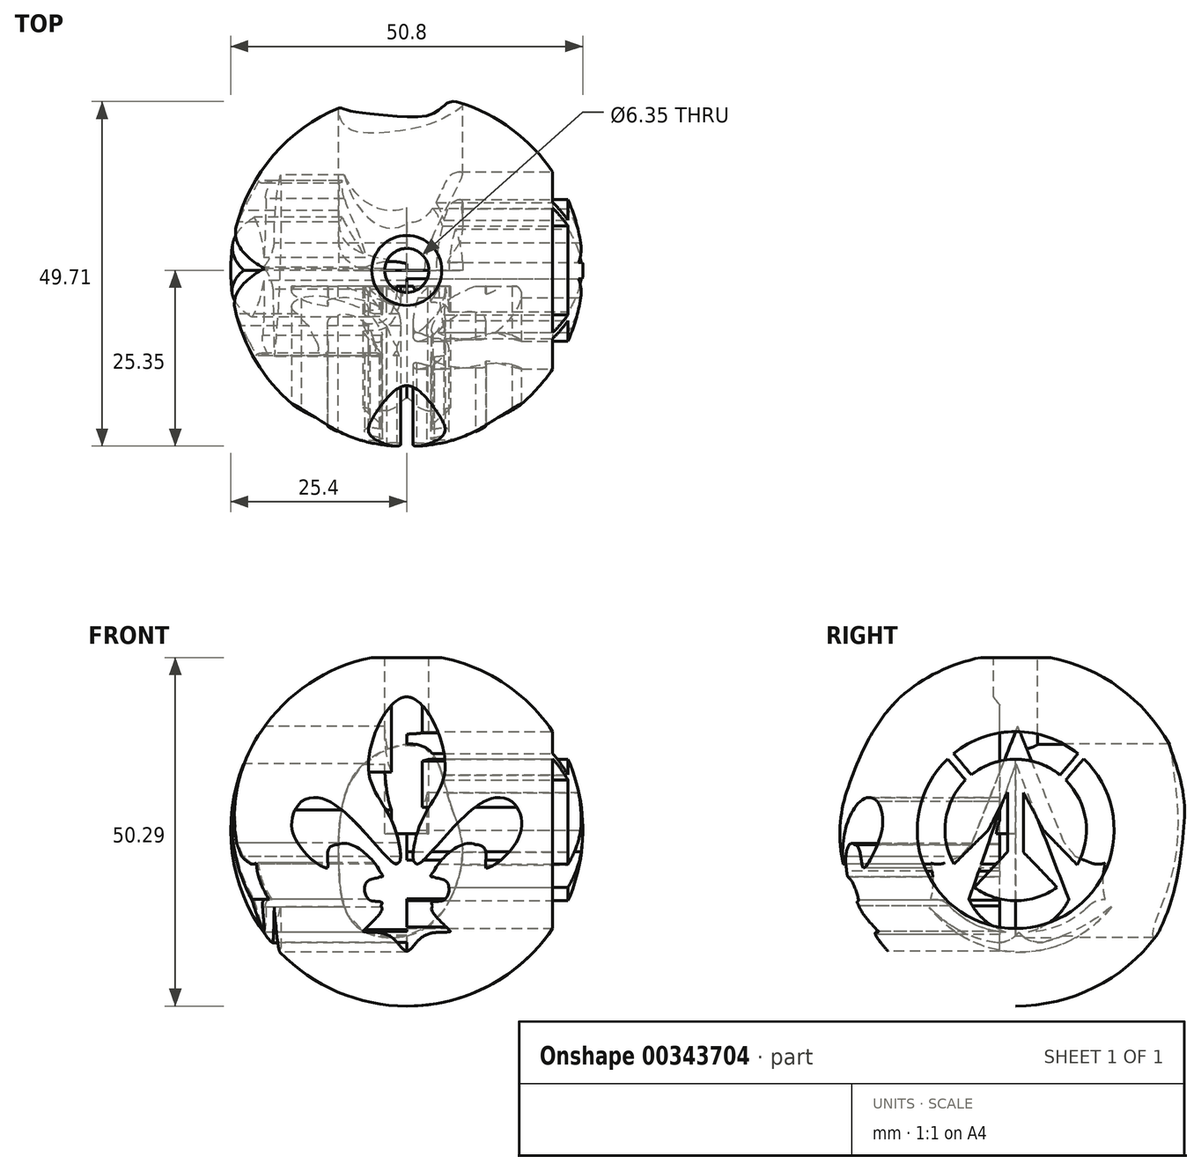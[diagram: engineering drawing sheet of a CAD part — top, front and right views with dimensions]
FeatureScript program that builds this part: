
annotation { "Feature Type Name" : "Feature", "Feature Type Description" : "" }
export const myFeature = defineFeature(function(context is Context, id is Id, definition is map)
    precondition{}
    {
        {
            var Q0;
            Q0=qCreatedBy(makeId("Front.planeOp"),FACE);
            var sketch = newSketch(context, id + "F0", { "sketchPlane" : qUnion([Q0])});
            skArc(sketch, "E0", {"start": v(0, 25.4) * mm, "mid": v(-25.4, 0) * mm, "end": v(0, -25.4) * mm});
            skLineSegment(sketch, "E1", {"start": v(0, 25.4) * mm, "end": v(0, -25.4) * mm});
            skPoint(sketch, "E2.orphan", {"position": v(0, 39.72) * mm});
            skSolve(sketch);
        }
        {
            var Q0;
            Q0=qCreatedBy(makeId("Top.planeOp"),FACE);
            var sketch = newSketch(context, id + "F1", { "sketchPlane" : qUnion([Q0])});
            skCircle(sketch, "E3", {"center": v(0, 0) * mm, "radius": 25.4 * mm});
            skSolve(sketch);
        }
        {
            var Q0;
            Q0=makeQuery(id+"F0.imprint","IMPRINT",FACE,{"disambiguationData":[TD([[makeQuery(id+"F0.imprint","IMPRINT",EDGE,{"derivedFrom":sQuery(id+"F0.wireOp",EDGE,"E0")}),1.0]])]});
            var Q1;
            Q1=sQuery(id+"F1.wireOp",EDGE,"E3");
            revolve(context, id + "F2", {"entities" : qUnion([Q0]), "axis" : qUnion([Q1]), "revolveType" : RevolveType.FULL});
        }
        {
            var Q0;
            Q0=qCreatedBy(makeId("Top.planeOp"),FACE);
            cPlane(context, id + "F3", {"entities" : qUnion([Q0]), "cplaneType" : CPlaneType.OFFSET, "offset" : 24.9 * mm, "width" : 152.4 * mm, "height" : 152.4 * mm});
        }
        {
            var Q0;
            Q0=qCreatedBy(id+"F3.planeOp",FACE);
            var sketch = newSketch(context, id + "F4", { "sketchPlane" : qUnion([Q0])});
            skLineSegment(sketch, "E4.bottom", {"start": v(-8.92, 8.63) * mm, "end": v(8.92, 8.63) * mm});
            skLineSegment(sketch, "E4.top", {"start": v(-8.92, -8.63) * mm, "end": v(8.92, -8.63) * mm});
            skLineSegment(sketch, "E4.left", {"start": v(-8.92, 8.63) * mm, "end": v(-8.92, -8.63) * mm});
            skLineSegment(sketch, "E4.right", {"start": v(8.92, 8.63) * mm, "end": v(8.92, -8.63) * mm});
            skPoint(sketch, "E4.middle", {"position": v(0, 0) * mm});
            skSolve(sketch);
        }
        {
            var Q0;
            Q0=makeQuery(id+"F4.imprint","IMPRINT",FACE,{"disambiguationData":[TD([[makeQuery(id+"F4.imprint","IMPRINT",EDGE,{"derivedFrom":sQuery(id+"F4.wireOp",EDGE,"E4.bottom")}),-1.0]])]});
            extrude(context, id + "F5", {"entities" : qUnion([Q0]), "operationType" : NewBodyOperationType.REMOVE, "depth" : 30.23 * mm});
        }
        {
            var Q0;
            Q0=qCreatedBy(makeId("Front.planeOp"),FACE);
            cPlane(context, id + "F6", {"entities" : qUnion([Q0]), "cplaneType" : CPlaneType.OFFSET, "offset" : 25.4 * mm, "width" : 152.4 * mm, "height" : 152.4 * mm});
        }
        {
            var Q0;
            Q0=qCreatedBy(id+"F6.planeOp",FACE);
            var sketch = newSketch(context, id + "F7", { "sketchPlane" : qUnion([Q0])});
            skFitSpline(sketch, "E5", {"points": [v(0, 19.2) * mm, v(-5.54, 9.35) * mm, v(-2.06, 1.1) * mm, v(-1.4, -4.9) * mm, v(-12.3, 4.57) * mm, v(-16.9, 0) * mm, v(-11.64, -5.75) * mm, v(-11.35, -3.03) * mm, v(-8.82, -2.38) * mm, v(-3.47, -6.7) * mm, v(-5.35, -6.88) * mm, v(-5.63, -9.98) * mm, v(-3.57, -10.54) * mm, v(-6.47, -14.39) * mm, v(-3, -15.04) * mm, v(0, -17.48) * mm, v(3, -15.04) * mm, v(6.57, -15.04) * mm, v(3.57, -11.38) * mm, v(5.54, -9.98) * mm, v(5.63, -7.35) * mm, v(3.85, -6.6) * mm, v(7.6, -2.28) * mm, v(10.6, -2.84) * mm, v(11.07, -5.47) * mm, v(16.51, 0) * mm, v(12.2, 4.85) * mm, v(1.5, -4.9) * mm, v(2.25, 1.28) * mm, v(5.54, 9.45) * mm, v(0, 19.2) * mm]});
            skFitSpline(sketch, "E6.MirrorC", {"points": [v(0, 19.2) * mm, v(5.54, 9.35) * mm, v(2.06, 1.1) * mm, v(1.4, -4.9) * mm, v(12.3, 4.57) * mm, v(16.9, 0) * mm, v(11.64, -5.75) * mm, v(11.35, -3.03) * mm, v(8.82, -2.38) * mm, v(3.47, -6.7) * mm, v(5.35, -6.88) * mm, v(5.63, -9.98) * mm, v(3.57, -10.54) * mm, v(6.47, -14.39) * mm, v(3, -15.04) * mm, v(0, -17.48) * mm, v(-3, -15.04) * mm, v(-6.57, -15.04) * mm, v(-3.57, -11.38) * mm, v(-5.54, -9.98) * mm, v(-5.63, -7.35) * mm, v(-3.85, -6.6) * mm, v(-7.6, -2.28) * mm, v(-10.6, -2.84) * mm, v(-11.07, -5.47) * mm, v(-16.51, 0) * mm, v(-12.2, 4.85) * mm, v(-1.5, -4.9) * mm, v(-2.25, 1.28) * mm, v(-5.54, 9.45) * mm, v(0, 19.2) * mm]});
            skSolve(sketch);
        }
        {
            var Q0;
            {var subQ1=sQuery(id+"F7.wireOp",EDGE,"E5");Q0=makeQuery(id+"F7.imprint","IMPRINT",FACE,{"disambiguationData":[TD([[makeQuery(id+"F7.imprint","IMPRINT",EDGE,{"derivedFrom":subQ1}),1.0]])]});}
            extrude(context, id + "F8", {"entities" : qUnion([Q0]), "operationType" : NewBodyOperationType.REMOVE, "oppositeDirection" : true, "depth" : 23.1 * mm});
        }
        {
            var Q0;
            Q0=qCreatedBy(makeId("Right.planeOp"),FACE);
            cPlane(context, id + "F9", {"entities" : qUnion([Q0]), "cplaneType" : CPlaneType.OFFSET, "offset" : 25.4 * mm, "width" : 152.4 * mm, "height" : 152.4 * mm});
        }
        {
            var Q0;
            Q0=qCreatedBy(id+"F9.planeOp",FACE);
            var sketch = newSketch(context, id + "F10", { "sketchPlane" : qUnion([Q0])});
            skArc(sketch, "E7", {"start": v(-9.82, 10.27) * mm, "mid": v(0, -14.2) * mm, "end": v(9.8, 10.28) * mm});
            skPoint(sketch, "E7.first.point", {"position": v(-6.94, 12.4) * mm});
            skPoint(sketch, "E7.second.point", {"position": v(6.62, -12.57) * mm});
            skPoint(sketch, "E7.third.point", {"position": v(-8.96, -11.02) * mm});
            skArc(sketch, "E8", {"start": v(-7.24, 7.2) * mm, "mid": v(0, -10.2) * mm, "end": v(7.23, 7.2) * mm});
            skLineSegment(sketch, "E9", {"start": v(8.87, -5.03) * mm, "end": v(3.98, 0) * mm});
            skLineSegment(sketch, "E10", {"start": v(3.98, 0) * mm, "end": v(1.13, 5.4) * mm});
            skLineSegment(sketch, "E11", {"start": v(1.13, 5.4) * mm, "end": v(1.13, -3.2) * mm});
            skLineSegment(sketch, "E12", {"start": v(1.13, -3.2) * mm, "end": v(5.97, -8.27) * mm});
            skLineSegment(sketch, "E13", {"start": v(-8.96, 11.03) * mm, "end": v(-6.38, 7.96) * mm});
            skLineSegment(sketch, "E14", {"start": v(-9.82, 10.27) * mm, "end": v(-7.24, 7.2) * mm});
            skLineSegment(sketch, "E15", {"start": v(8.99, 11) * mm, "end": v(6.4, 7.94) * mm});
            skLineSegment(sketch, "E16", {"start": v(9.8, 10.28) * mm, "end": v(7.23, 7.2) * mm});
            skPoint(sketch, "E17.start.orphan", {"position": v(-3.94, 0) * mm});
            skLineSegment(sketch, "E18", {"start": v(-8.93, -4.94) * mm, "end": v(-3.94, 0) * mm});
            skLineSegment(sketch, "E19", {"start": v(-3.94, 0) * mm, "end": v(-1.18, 5.45) * mm});
            skLineSegment(sketch, "E20", {"start": v(-1.18, 5.45) * mm, "end": v(-1.18, -3.15) * mm});
            skLineSegment(sketch, "E21", {"start": v(-5.97, -8.27) * mm, "end": v(-1.18, -3.15) * mm});
            skArc(sketch, "E22.trimOffspring", {"start": v(6.4, 7.94) * mm, "mid": v(0.01, 10.2) * mm, "end": v(-6.38, 7.96) * mm});
            skArc(sketch, "E23.trimOffspring", {"start": v(8.99, 11) * mm, "mid": v(0.02, 14.2) * mm, "end": v(-8.96, 11.03) * mm});
            skSolve(sketch);
        }
        {
            var Q0;
            Q0=makeQuery(id+"F10.imprint","IMPRINT",FACE,{"disambiguationData":[TD([[makeQuery(id+"F10.imprint","IMPRINT",EDGE,{"derivedFrom":sQuery(id+"F10.wireOp",EDGE,"E13")}),1.0]])]});
            var Q1;
            Q1=makeQuery(id+"F10.imprint","IMPRINT",FACE,{"disambiguationData":[TD([[makeQuery(id+"F10.imprint","IMPRINT",EDGE,{"derivedFrom":sQuery(id+"F10.wireOp",EDGE,"E7")}),1.0]])]});
            var Q2;
            {var subQ0=sQuery(id+"F10.wireOp",EDGE,"E18");Q2=makeQuery(id+"F10.imprint","IMPRINT",FACE,{"disambiguationData":[TD([[makeQuery(id+"F10.imprint","IMPRINT",EDGE,{"derivedFrom":subQ0}),-1.0]])]});}
            var Q3;
            {var subQ0=sQuery(id+"F10.wireOp",EDGE,"E9");Q3=makeQuery(id+"F10.imprint","IMPRINT",FACE,{"disambiguationData":[TD([[makeQuery(id+"F10.imprint","IMPRINT",EDGE,{"derivedFrom":subQ0}),1.0]])]});}
            extrude(context, id + "F11", {"entities" : qUnion([Q0, Q1, Q2, Q3]), "operationType" : NewBodyOperationType.REMOVE, "oppositeDirection" : true, "depth" : 25.4 * mm});
        }
        {
            var Q0;
            Q0=qCreatedBy(makeId("Right.planeOp"),FACE);
            cPlane(context, id + "F12", {"entities" : qUnion([Q0]), "cplaneType" : CPlaneType.OFFSET, "offset" : 25.4 * mm, "oppositeDirection" : true, "width" : 152.4 * mm, "height" : 152.4 * mm});
        }
        {
            var Q0;
            Q0=qCreatedBy(makeId("Front.planeOp"),FACE);
            cPlane(context, id + "F13", {"entities" : qUnion([Q0]), "cplaneType" : CPlaneType.OFFSET, "offset" : 25.4 * mm, "oppositeDirection" : true, "width" : 152.4 * mm, "height" : 152.4 * mm});
        }
        {
            var Q0;
            Q0=qCreatedBy(id+"F13.planeOp",FACE);
            var sketch = newSketch(context, id + "F14", { "sketchPlane" : qUnion([Q0])});
            skFitSpline(sketch, "E24", {"points": [v(8.06, -2.66) * mm, v(6.21, 4) * mm, v(2.95, 11.74) * mm, v(-4.2, 11.02) * mm, v(-8.8, 5.45) * mm, v(-9.79, -5.32) * mm, v(-7.1, -14.03) * mm, v(3.07, -13.91) * mm, v(8.06, -2.66) * mm]});
            skSolve(sketch);
        }
        {
            var Q0;
            Q0=makeQuery(id+"F14.imprint","IMPRINT",FACE,{"disambiguationData":[TD([[makeQuery(id+"F14.imprint","IMPRINT",EDGE,{"derivedFrom":sQuery(id+"F14.wireOp",EDGE,"E24")}),1.0]])]});
            extrude(context, id + "F15", {"entities" : qUnion([Q0]), "operationType" : NewBodyOperationType.REMOVE, "depth" : 25.4 * mm});
        }
        {
            var Q0;
            Q0=qCreatedBy(id+"F12.planeOp",FACE);
            var sketch = newSketch(context, id + "F16", { "sketchPlane" : qUnion([Q0])});
            skLineSegment(sketch, "E25", {"start": v(0.29, 14.97) * mm, "end": v(7, -1.84) * mm});
            skLineSegment(sketch, "E26", {"start": v(0.29, 14.97) * mm, "end": v(-6.3, -1.9) * mm});
            skLineSegment(sketch, "E27", {"start": v(-6.3, -1.9) * mm, "end": v(-8.02, -3.86) * mm});
            skLineSegment(sketch, "E28", {"start": v(-8.02, -3.86) * mm, "end": v(-10.22, -4.74) * mm});
            skLineSegment(sketch, "E29", {"start": v(7, -1.84) * mm, "end": v(8.66, -3.86) * mm});
            skLineSegment(sketch, "E30", {"start": v(8.66, -3.86) * mm, "end": v(10.86, -4.74) * mm});
            skArc(sketch, "E31", {"start": v(10.86, -4.74) * mm, "mid": v(11.9, -4.94) * mm, "end": v(12.94, -4.74) * mm});
            skArc(sketch, "E32", {"start": v(-12.3, -4.74) * mm, "mid": v(-11.26, -4.94) * mm, "end": v(-10.22, -4.74) * mm});
            skArc(sketch, "E33", {"start": v(12.94, -4.74) * mm, "mid": v(12.59, -7.38) * mm, "end": v(12.94, -10.02) * mm});
            skArc(sketch, "E34", {"start": v(-12.3, -10.02) * mm, "mid": v(-11.95, -7.38) * mm, "end": v(-12.3, -4.74) * mm});
            skArc(sketch, "E35", {"start": v(12.94, -10.02) * mm, "mid": v(11.52, -10.27) * mm, "end": v(10.38, -11.13) * mm});
            skArc(sketch, "E36", {"start": v(-9.39, -11.13) * mm, "mid": v(-10.7, -10.18) * mm, "end": v(-12.3, -10.02) * mm});
            skArc(sketch, "E37", {"start": v(1.82, -14.72) * mm, "mid": v(6.43, -13.71) * mm, "end": v(10.38, -11.13) * mm});
            skArc(sketch, "E38", {"start": v(-9.39, -11.13) * mm, "mid": v(-5.76, -13.7) * mm, "end": v(-1.43, -14.72) * mm});
            skArc(sketch, "E39", {"start": v(-6.74, -10.02) * mm, "mid": v(-4.58, -12.93) * mm, "end": v(-1.43, -14.72) * mm});
            skArc(sketch, "E40", {"start": v(1.82, -14.72) * mm, "mid": v(5.28, -13.03) * mm, "end": v(7.68, -10.02) * mm});
            skLineSegment(sketch, "E41", {"start": v(7.68, -10.02) * mm, "end": v(0.02, 9.58) * mm});
            skLineSegment(sketch, "E42", {"start": v(0.02, 9.58) * mm, "end": v(-6.74, -10.02) * mm});
            skArc(sketch, "E43", {"start": v(0.45, -14.72) * mm, "mid": v(2, -15.9) * mm, "end": v(3.92, -16.2) * mm});
            skArc(sketch, "E44", {"start": v(-2.71, -16.27) * mm, "mid": v(-0.95, -15.87) * mm, "end": v(0.45, -14.72) * mm});
            skArc(sketch, "E45", {"start": v(3.92, -16.2) * mm, "mid": v(9.15, -14.17) * mm, "end": v(13.81, -11.05) * mm});
            skArc(sketch, "E46", {"start": v(-12.47, -11.13) * mm, "mid": v(-8.04, -14.55) * mm, "end": v(-2.71, -16.27) * mm});
            skArc(sketch, "E47", {"start": v(-12.47, -11.13) * mm, "mid": v(0.7, -17.6) * mm, "end": v(13.81, -11.05) * mm});
            skSolve(sketch);
        }
        {
            var Q0;
            Q0=makeQuery(id+"F16.imprint","IMPRINT",FACE,{"disambiguationData":[TD([[makeQuery(id+"F16.imprint","IMPRINT",EDGE,{"derivedFrom":sQuery(id+"F16.wireOp",EDGE,"E25")}),-1.0]])]});
            var Q1;
            Q1=makeQuery(id+"F16.imprint","IMPRINT",FACE,{"disambiguationData":[TD([[makeQuery(id+"F16.imprint","IMPRINT",EDGE,{"derivedFrom":sQuery(id+"F16.wireOp",EDGE,"E43")}),-1.0]])]});
            extrude(context, id + "F17", {"entities" : qUnion([Q0, Q1]), "operationType" : NewBodyOperationType.REMOVE, "depth" : 25.4 * mm});
        }
        {
            var Q0;
            Q0=makeQuery(id+"F5.boolean.opBoolean","COPY",FACE,{"derivedFrom":makeQuery(id+"F5.opExtrude","CAP_FACE",FACE,{"disambiguationData":[OSD([sQuery(id+"F4.wireOp",EDGE,"E4.bottom"),sQuery(id+"F4.wireOp",EDGE,"E4.top"),sQuery(id+"F4.wireOp",EDGE,"E4.left"),sQuery(id+"F4.wireOp",EDGE,"E4.right")])],"isStart":true})});
            var sketch = newSketch(context, id + "F18", { "sketchPlane" : qUnion([Q0])});
            skCircle(sketch, "E48", {"center": v(0, 0) * mm, "radius": 3.18 * mm});
            skSolve(sketch);
        }
        {
            var Q0;
            Q0=makeQuery(id+"F18.imprint","IMPRINT",FACE,{"disambiguationData":[TD([[makeQuery(id+"F18.imprint","IMPRINT",EDGE,{"derivedFrom":sQuery(id+"F18.wireOp",EDGE,"E48")}),1.0]])]});
            extrude(context, id + "F19", {"entities" : qUnion([Q0]), "operationType" : NewBodyOperationType.REMOVE, "oppositeDirection" : true, "depth" : 25.4 * mm});
        }
    });
